# Revit family: ElectricalFixtures_WiringAccessories_Hager_Sollysta_ShowerSwitches
name_source: partatom
category: Lighting Fixtures
revit_build: Autodesk Revit 2015 (Build: 20160512_1515(x64)
units: mm (PartAtom-declared; Revit-internal decimal feet)

## types (1)
- WMCS50N
    CE Approval = Yes
    Colour = SollystaWhite
    Description = 50ADPCeilingSwitchWithLEDIndicator
    Design Country = China
    EAN Code = 5015652260233
    Expected Life = 25
    Features = 50ADPCeilingSwitchWithLEDIndicator
    Finish = Gloss
    Frequency = 50/60Hz
    Manufacturer = Hager
    Manufacturer Country = UnitedKingdom
    Manufacturer Website = http://www.hager.co.uk
    Material = Urea Formaldehyde Thermoset Plastic
    Name = WhiteMouldedCeilingSwitches_ShowerSwitches_WMCS50N
    Overall Depth = 50 mm  [stored 0.164042 ft]
    Overall Height = 0 mm  [stored 0 ft]
    Overall Width = 100 mm  [stored 0.328084 ft]
    Packaging Recyclable = Yes
    Product Family = WhiteMouldedCeilingSwitches
    Product Group = FanIsolatorSwitches
    Product Literature = http://www.hager.co.uk
    Product Model Number = WMCS50N
    Product Range = WhiteMouldedCeilingSwitches_FanIsolatorSwitches
    Product URL = http://www.hager.co.uk
    Reference Standard = BS 1363-2
    Shape = Circular
    Supply Phase = 1
    Technical Description = 50ADPCeilingSwitchWithLEDIndicator
    Type = ElectricalFixture
    URL = http://www.hager.co.uk
    Unique Reference = WMCS50N
    Voltage (Volts) = 230V/240V

note: [stored X ft] marks values corroborated as IEEE doubles in the binary element streams (Revit-internal decimal feet)

## geometry (parser evidence)
native form markers: Blend x4, Sweep x2
no freeform markers — native parametric forms only
